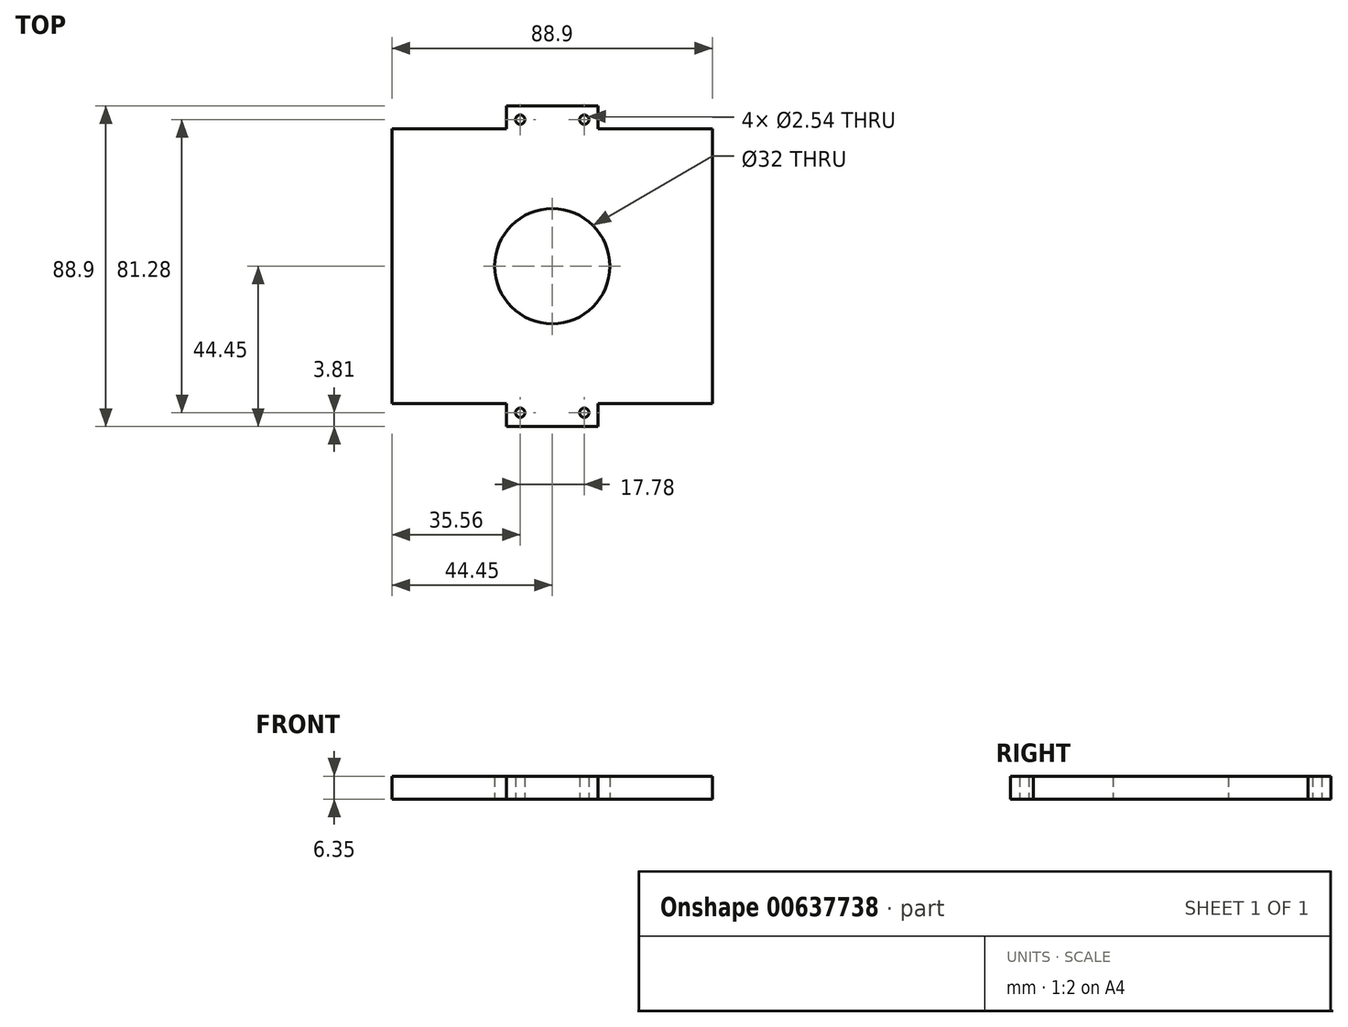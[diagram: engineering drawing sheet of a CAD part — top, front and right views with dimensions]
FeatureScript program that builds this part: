
annotation { "Feature Type Name" : "Feature", "Feature Type Description" : "" }
export const myFeature = defineFeature(function(context is Context, id is Id, definition is map)
    precondition{}
    {
        {
            var Q0;
            Q0=qCreatedBy(makeId("Top.planeOp"),FACE);
            var sketch = newSketch(context, id + "F0", { "sketchPlane" : qUnion([Q0])});
            skLineSegment(sketch, "E0.bottom", {"start": v(0, 0) * mm, "end": v(-88.9, 0) * mm});
            skLineSegment(sketch, "E0.top", {"start": v(0, 76.2) * mm, "end": v(-88.9, 76.2) * mm});
            skLineSegment(sketch, "E0.left", {"start": v(0, 0) * mm, "end": v(0, 76.2) * mm});
            skLineSegment(sketch, "E0.right", {"start": v(-88.9, 0) * mm, "end": v(-88.9, 76.2) * mm});
            skLineSegment(sketch, "E1", {"start": v(0, 38.1) * mm, "end": v(-44.45, 38.1) * mm});
            skCircle(sketch, "E2", {"center": v(-44.45, 38.1) * mm, "radius": 16 * mm});
            skLineSegment(sketch, "E3.bottom", {"start": v(-57.15, 82.55) * mm, "end": v(-31.75, 82.55) * mm});
            skLineSegment(sketch, "E3.left", {"start": v(-57.15, 82.55) * mm, "end": v(-57.15, 76.2) * mm});
            skLineSegment(sketch, "E3.right", {"start": v(-31.75, 82.55) * mm, "end": v(-31.75, 76.2) * mm});
            skPoint(sketch, "E3.middle", {"position": v(-44.45, 76.2) * mm});
            skLineSegment(sketch, "E4.bottom", {"start": v(-57.15, 76.2) * mm, "end": v(-53.34, 76.2) * mm});
            skLineSegment(sketch, "E4.top", {"start": v(-54.61, 78.74) * mm, "end": v(-53.34, 78.74) * mm});
            skLineSegment(sketch, "E4.left", {"start": v(-57.15, 76.2) * mm, "end": v(-57.15, 78.74) * mm});
            skLineSegment(sketch, "E4.right", {"start": v(-53.34, 77.47) * mm, "end": v(-53.34, 78.74) * mm});
            skLineSegment(sketch, "E5.bottom", {"start": v(-31.75, 76.2) * mm, "end": v(-35.56, 76.2) * mm});
            skLineSegment(sketch, "E5.top", {"start": v(-34.3, 78.74) * mm, "end": v(-35.56, 78.74) * mm});
            skLineSegment(sketch, "E5.left", {"start": v(-31.75, 76.2) * mm, "end": v(-31.75, 78.74) * mm});
            skLineSegment(sketch, "E5.right", {"start": v(-35.56, 77.47) * mm, "end": v(-35.56, 78.74) * mm});
            skCircle(sketch, "E6", {"center": v(-53.34, 78.74) * mm, "radius": 1.27 * mm});
            skCircle(sketch, "E7", {"center": v(-35.56, 78.74) * mm, "radius": 1.27 * mm});
            skPoint(sketch, "E8.orphan", {"position": v(-57.15, 69.85) * mm});
            skPoint(sketch, "E9.orphan", {"position": v(-31.75, 69.85) * mm});
            skLineSegment(sketch, "E10.bottom", {"start": v(-57.15, -6.35) * mm, "end": v(-31.75, -6.35) * mm});
            skLineSegment(sketch, "E10.left", {"start": v(-57.15, -6.35) * mm, "end": v(-57.15, 0) * mm});
            skLineSegment(sketch, "E10.right", {"start": v(-31.75, -6.35) * mm, "end": v(-31.75, 0) * mm});
            skPoint(sketch, "E10.middle", {"position": v(-44.45, 0) * mm});
            skLineSegment(sketch, "E11.bottom", {"start": v(-57.15, 0) * mm, "end": v(-53.34, 0) * mm});
            skLineSegment(sketch, "E11.top", {"start": v(-54.6, -2.54) * mm, "end": v(-53.34, -2.54) * mm});
            skLineSegment(sketch, "E11.left", {"start": v(-57.15, 0) * mm, "end": v(-57.15, -2.54) * mm});
            skLineSegment(sketch, "E11.right", {"start": v(-53.34, -1.27) * mm, "end": v(-53.34, -2.54) * mm});
            skLineSegment(sketch, "E12.bottom", {"start": v(-31.75, 0) * mm, "end": v(-35.56, 0) * mm});
            skLineSegment(sketch, "E12.top", {"start": v(-34.29, -2.54) * mm, "end": v(-35.56, -2.54) * mm});
            skLineSegment(sketch, "E12.left", {"start": v(-31.75, 0) * mm, "end": v(-31.75, -2.54) * mm});
            skLineSegment(sketch, "E12.right", {"start": v(-35.56, -1.27) * mm, "end": v(-35.56, -2.54) * mm});
            skCircle(sketch, "E13", {"center": v(-53.34, -2.54) * mm, "radius": 1.27 * mm});
            skCircle(sketch, "E14", {"center": v(-35.56, -2.54) * mm, "radius": 1.27 * mm});
            skPoint(sketch, "E15.orphan", {"position": v(-31.75, 6.35) * mm});
            skPoint(sketch, "E16.orphan", {"position": v(-57.15, 6.35) * mm});
            skSolve(sketch);
        }
        {
            var Q0;
            {var subQ3=sQuery(id+"F0.wireOp",EDGE,"E0.bottom");Q0=makeQuery(id+"F0.imprint","IMPRINT",FACE,{"disambiguationData":[TD([[makeQuery(id+"F0.imprint","IMPRINT",EDGE,{"derivedFrom":subQ3}),-1.0]])]});}
            var Q1;
            Q1=makeQuery(id+"F0.imprint","IMPRINT",FACE,{"disambiguationData":[TD([[makeQuery(id+"F0.imprint","IMPRINT",EDGE,{"derivedFrom":sQuery(id+"F0.wireOp",EDGE,"E3.bottom")}),-1.0]])]});
            var Q2;
            Q2=makeQuery(id+"F0.imprint","IMPRINT",FACE,{"disambiguationData":[TD([[makeQuery(id+"F0.imprint","IMPRINT",EDGE,{"derivedFrom":sQuery(id+"F0.wireOp",EDGE,"E10.bottom")}),1.0]])]});
            extrude(context, id + "F1", {"entities" : qUnion([Q0, Q1, Q2]), "depth" : 6.35 * mm, "offsetDistance" : 25.4 * mm});
        }
    });
